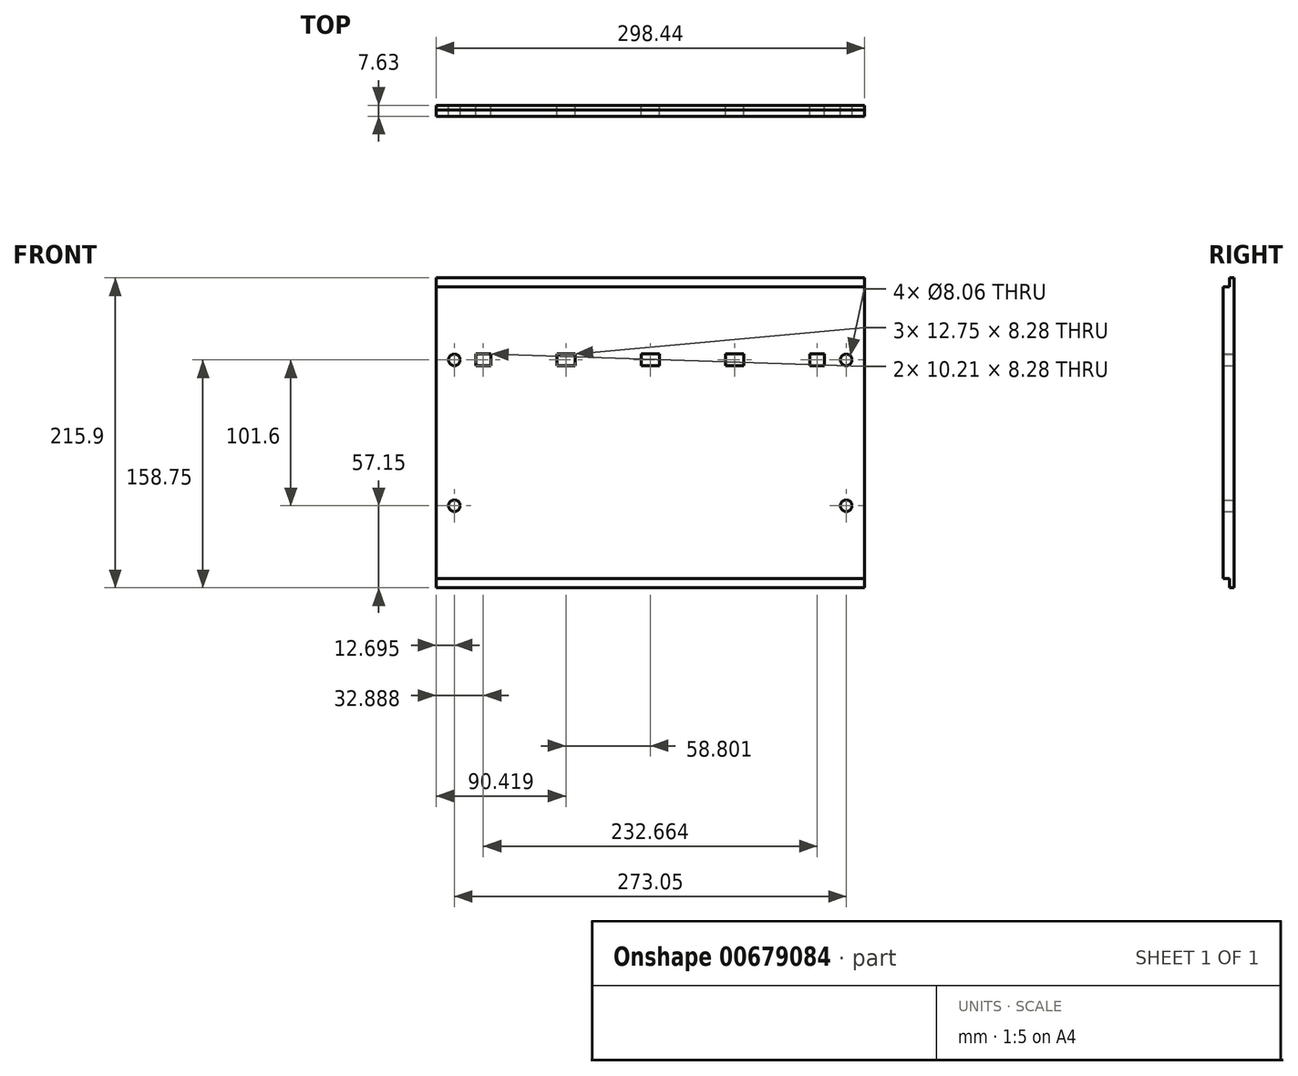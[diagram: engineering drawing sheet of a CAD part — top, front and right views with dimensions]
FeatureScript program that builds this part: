
annotation { "Feature Type Name" : "Feature", "Feature Type Description" : "" }
export const myFeature = defineFeature(function(context is Context, id is Id, definition is map)
    precondition{}
    {
        {
            var Q0;
            Q0=qCreatedBy(makeId("Front.planeOp"),FACE);
            var sketch = newSketch(context, id + "F0", { "sketchPlane" : qUnion([Q0])});
            skLineSegment(sketch, "E0.bottom", {"start": v(-149.22, 107.95) * mm, "end": v(149.23, 107.95) * mm});
            skLineSegment(sketch, "E0.top", {"start": v(-149.23, -107.95) * mm, "end": v(149.22, -107.95) * mm});
            skLineSegment(sketch, "E0.left", {"start": v(-149.22, 107.95) * mm, "end": v(-149.23, -107.95) * mm});
            skLineSegment(sketch, "E0.right", {"start": v(149.23, 107.95) * mm, "end": v(149.22, -107.95) * mm});
            skPoint(sketch, "E0.middle", {"position": v(0, 0) * mm});
            skLineSegment(sketch, "E1.bottom", {"start": v(-149.23, 101.6) * mm, "end": v(149.23, 101.6) * mm});
            skLineSegment(sketch, "E1.top", {"start": v(-149.23, -101.6) * mm, "end": v(149.23, -101.6) * mm});
            skLineSegment(sketch, "E1.left", {"start": v(-149.23, 101.6) * mm, "end": v(-149.23, -101.6) * mm});
            skLineSegment(sketch, "E1.right", {"start": v(149.23, 101.6) * mm, "end": v(149.23, -101.6) * mm});
            skCircle(sketch, "E2", {"center": v(136.53, -50.8) * mm, "radius": 4.03 * mm});
            skCircle(sketch, "E3", {"center": v(136.53, 50.8) * mm, "radius": 4.03 * mm});
            skCircle(sketch, "E4", {"center": v(-136.53, 50.8) * mm, "radius": 4.03 * mm});
            skCircle(sketch, "E5", {"center": v(-136.53, -50.8) * mm, "radius": 4.03 * mm});
            skLineSegment(sketch, "E6.bottom", {"start": v(-6.38, 46.66) * mm, "end": v(6.38, 46.66) * mm});
            skLineSegment(sketch, "E6.top", {"start": v(-6.38, 54.94) * mm, "end": v(6.38, 54.94) * mm});
            skLineSegment(sketch, "E6.left", {"start": v(-6.38, 46.66) * mm, "end": v(-6.38, 54.94) * mm});
            skLineSegment(sketch, "E6.right", {"start": v(6.38, 46.66) * mm, "end": v(6.38, 54.94) * mm});
            skPoint(sketch, "E6.middle", {"position": v(0, 50.8) * mm});
            skLineSegment(sketch, "E7.bottom", {"start": v(52.43, 46.66) * mm, "end": v(65.18, 46.66) * mm});
            skLineSegment(sketch, "E7.top", {"start": v(52.43, 54.94) * mm, "end": v(65.18, 54.94) * mm});
            skLineSegment(sketch, "E7.left", {"start": v(52.43, 46.66) * mm, "end": v(52.43, 54.94) * mm});
            skLineSegment(sketch, "E7.right", {"start": v(65.18, 46.66) * mm, "end": v(65.18, 54.94) * mm});
            skPoint(sketch, "E7.middle", {"position": v(58.8, 50.8) * mm});
            skLineSegment(sketch, "E8.bottom", {"start": v(-65.18, 46.66) * mm, "end": v(-52.43, 46.66) * mm});
            skLineSegment(sketch, "E8.top", {"start": v(-65.18, 54.94) * mm, "end": v(-52.43, 54.94) * mm});
            skLineSegment(sketch, "E8.left", {"start": v(-65.18, 46.66) * mm, "end": v(-65.18, 54.94) * mm});
            skLineSegment(sketch, "E8.right", {"start": v(-52.43, 46.66) * mm, "end": v(-52.43, 54.94) * mm});
            skPoint(sketch, "E8.middle", {"position": v(-58.8, 50.8) * mm});
            skLineSegment(sketch, "E9.bottom", {"start": v(-121.44, 46.66) * mm, "end": v(-111.23, 46.66) * mm});
            skLineSegment(sketch, "E9.top", {"start": v(-121.44, 54.94) * mm, "end": v(-111.23, 54.94) * mm});
            skLineSegment(sketch, "E9.left", {"start": v(-121.44, 46.66) * mm, "end": v(-121.44, 54.94) * mm});
            skLineSegment(sketch, "E9.right", {"start": v(-111.23, 46.66) * mm, "end": v(-111.23, 54.94) * mm});
            skPoint(sketch, "E9.middle", {"position": v(-116.33, 50.8) * mm});
            skLineSegment(sketch, "E10.bottom", {"start": v(111.23, 46.66) * mm, "end": v(121.44, 46.66) * mm});
            skLineSegment(sketch, "E10.top", {"start": v(111.23, 54.94) * mm, "end": v(121.44, 54.94) * mm});
            skLineSegment(sketch, "E10.left", {"start": v(111.23, 46.66) * mm, "end": v(111.23, 54.94) * mm});
            skLineSegment(sketch, "E10.right", {"start": v(121.44, 46.66) * mm, "end": v(121.44, 54.94) * mm});
            skPoint(sketch, "E10.middle", {"position": v(116.33, 50.8) * mm});
            skSolve(sketch);
        }
        {
            var Q0;
            Q0=makeQuery(id+"F0.imprint","IMPRINT",FACE,{"disambiguationData":[TD([[makeQuery(id+"F0.imprint","IMPRINT",EDGE,{"derivedFrom":sQuery(id+"F0.wireOp",EDGE,"E1.bottom")}),-1.0]])]});
            extrude(context, id + "F1", {"entities" : qUnion([Q0]), "depth" : 4.44 * mm, "offsetDistance" : 25.4 * mm});
        }
        {
            var Q0;
            Q0=makeQuery(id+"F0.imprint","IMPRINT",FACE,{"disambiguationData":[TD([[makeQuery(id+"F0.imprint","IMPRINT",EDGE,{"derivedFrom":sQuery(id+"F0.wireOp",EDGE,"E0.bottom")}),-1.0]])]});
            var Q1;
            Q1=makeQuery(id+"F0.imprint","IMPRINT",FACE,{"disambiguationData":[TD([[makeQuery(id+"F0.imprint","IMPRINT",EDGE,{"derivedFrom":sQuery(id+"F0.wireOp",EDGE,"E1.bottom")}),-1.0]])]});
            var Q2;
            {var subQ0=sQuery(id+"F0.wireOp",EDGE,"E0.top");Q2=makeQuery(id+"F0.imprint","IMPRINT",FACE,{"disambiguationData":[TD([[makeQuery(id+"F0.imprint","IMPRINT",EDGE,{"derivedFrom":subQ0}),1.0]])]});}
            extrude(context, id + "F2", {"entities" : qUnion([Q0, Q1, Q2]), "operationType" : NewBodyOperationType.ADD, "depth" : -3.17 * mm, "offsetDistance" : 25.4 * mm});
        }
    });
